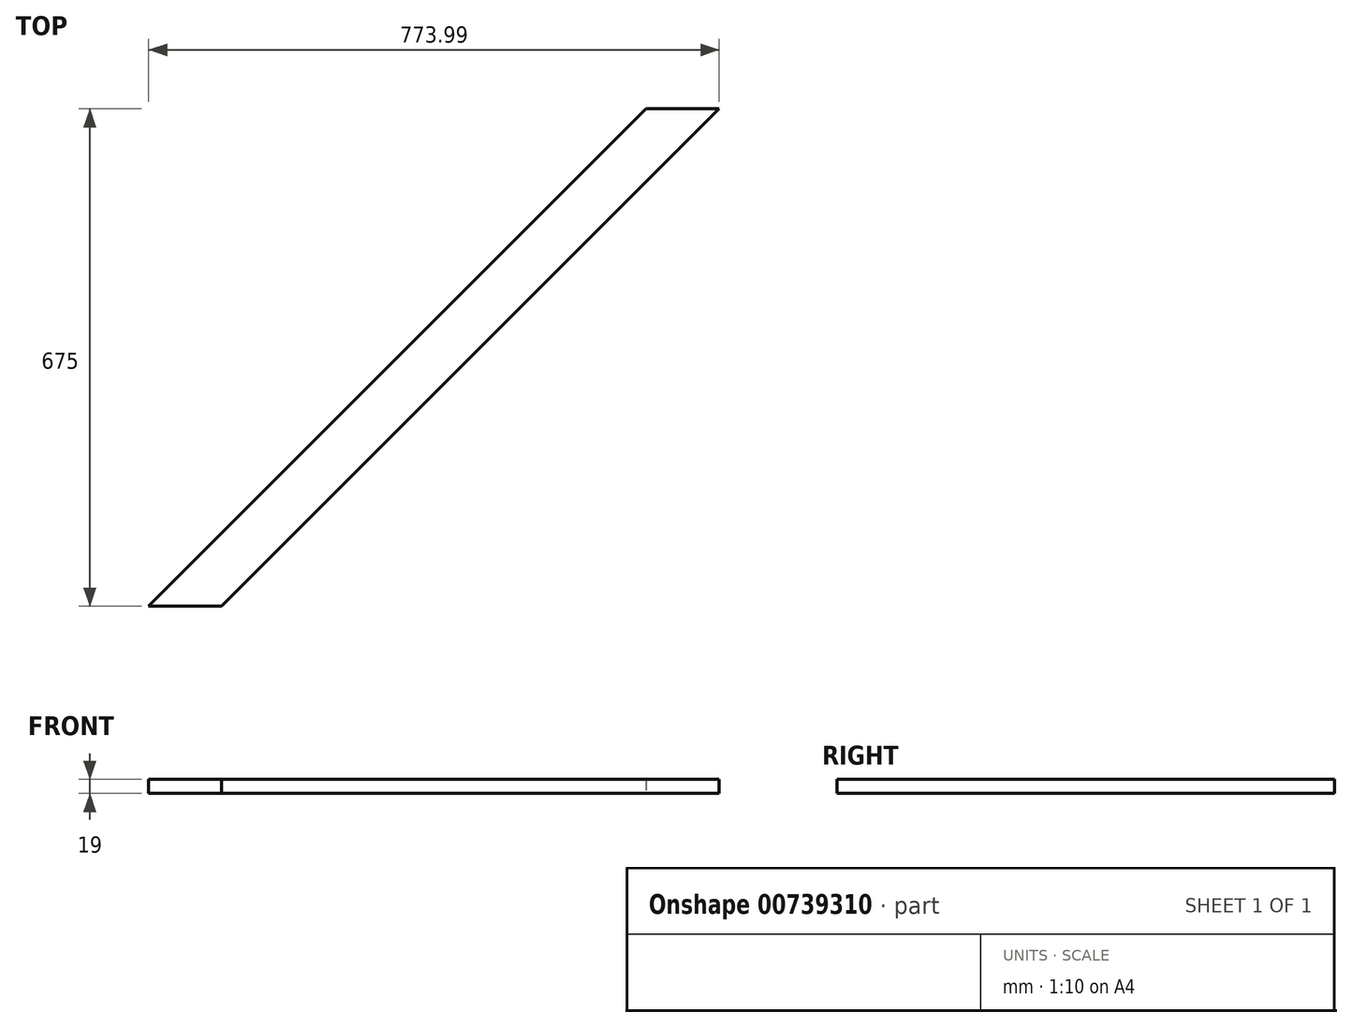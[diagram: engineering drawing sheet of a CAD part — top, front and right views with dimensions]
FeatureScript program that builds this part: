
annotation { "Feature Type Name" : "Feature", "Feature Type Description" : "" }
export const myFeature = defineFeature(function(context is Context, id is Id, definition is map)
    precondition{}
    {
        {
            var Q0;
            Q0=qCreatedBy(makeId("Top.planeOp"),FACE);
            var sketch = newSketch(context, id + "F0", { "sketchPlane" : qUnion([Q0])});
            skLineSegment(sketch, "E0", {"start": v(0, 0) * mm, "end": v(99, 0) * mm});
            skLineSegment(sketch, "E1", {"start": v(99, 0) * mm, "end": v(774, 675) * mm});
            skLineSegment(sketch, "E2", {"start": v(774, 675) * mm, "end": v(675, 675) * mm});
            skLineSegment(sketch, "E3", {"start": v(675, 675) * mm, "end": v(0, 0) * mm});
            skSolve(sketch);
        }
        {
            var Q0;
            Q0=makeQuery(id+"F0.imprint","IMPRINT",FACE,{"disambiguationData":[TD([[makeQuery(id+"F0.imprint","IMPRINT",EDGE,{"derivedFrom":sQuery(id+"F0.wireOp",EDGE,"E0")}),1.0]])]});
            extrude(context, id + "F1", {"entities" : qUnion([Q0]), "depth" : 19 * mm, "offsetDistance" : 25 * mm});
        }
    });
